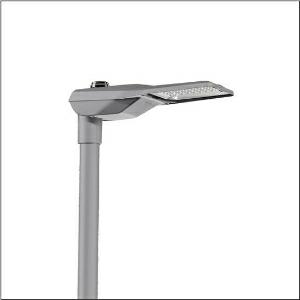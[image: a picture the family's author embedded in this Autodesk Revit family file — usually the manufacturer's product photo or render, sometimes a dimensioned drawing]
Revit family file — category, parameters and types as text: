
# Revit family: streetlight_sl_21_mini___st0_5a_5xe6b47n08hb_7d81
name_source: partatom
category: Lighting Fixtures
units: mm (PartAtom-declared; Revit-internal decimal feet)

## family parameters
Cut with Voids When Loaded = No
Host = Face
Light Source = No
Part Type = Normal
Room Calculation Point = No
Round Connector Dimension = Use Diameter
Shared = No

## types (1)
- --- (1 x LED, 9430 lm, 66 W, 4000K)
    Apparent Load = 66 VA
    CIE Flux Codes = 41 75 97 100 100
    Color Rendering = 70
    Color Temperature = 4000K
    Default Elevation = 1800 mm
    Description = Streetlight SL 21 mini, mast luminaire, primary light control with lens, of PMMA, primary optical cover: cover, of toughened safety glass, transparent, light distribution: ST0.5a, light emission: direct distribution, primary light characteristic: asymmetric, installation type: side-entry, LED, 3G 1.5mm², High Power LED, rated luminous flux: 9.430lm, luminous efficacy: 143lm/W, light colour: 740, colour temperature: 4000K, control gear: NEMA (7pin), control: overheat protection, pre-setting: linear dimming characteristic, constant luminous flux control, time-dependent luminous flux control, flexible luminous flux parameterisation, mains connection: 230..240V, AC, 50/60Hz, connection cable pre-assembled, cable length: 8,5m, wiring characteristics: H07RN-F, start of lifetime: 66W, end of service life: 69W, reduction: 30W, luminaire housing, of diecast aluminium (EN AC-44300), powder-coated, SITECO metallic grey (DB 702S), corrosivity category C5 high according to DIN EN ISO 12944, multi-level sealing system, sealing non-destructively replaceable, inclination adjustable: 0°, 5°, 10°, 15°, length: 628mm, width: 235mm, height: 110mm, spigot size: 42mm (side-entry), mounting height: 4..8m, protection rating (complete): IP66, insulation class (complete): insulation class I (protective earthing), certification: CE, ENEC, ENEC+, VDE, impact resistance: IK10, permissible operating ambient temperature for outdoor applications: -40..+50°C, standard-compliant lighting for roads and squares, packaging unit: 1 piece

Light Distribution: ST0.5a
    Height = 110 mm
    Lamp = 1 x LED
    Lamp Light Flux = 9430 lm
    Lamp Power = 66 W
    Lamp count = 1
    Length = 625 mm
    Luminous efficacy = 143 lm/W
    Manufacturer = Siteco
    ModVariant = No
    Model = 5XE6B47N08HB
    Number of Poles = 1
    OnlyDefault = Yes
    Power Factor = 1
    Product Name = Streetlight SL 21 mini | ST0.5a
    Product group = mast luminaire | pylon top
    ProductGroupID = 6100
    Protection Class = Protection class I
    Protection Degree = IP 66
    RLX_Detail_Level = 1
    RLX_Emergency_Light_Flux = 0 lm
    RLX_Emergency_Type = 0
    RLX_Emergency_Type_DB = No
    RlxData = <blob elided: 37161 chars, md5=1969a951>
    Socket = socket
    Standby Power = 0 W
    System Light Flux = 9430 lm
    System Power = 66 W
    Type Comments = factory setting: luminous flux: 100 % | dim-lin: 254 | 670 mA
    Type Image = l_1294379.jpg
    URL = http://relux.com
    VarID = @adj_136913
    Voltage = 0 V
    Weight = 0.00 kg
    Width = 234 mm

## geometry (parser evidence)
native form markers: Blend x4, Sweep x12
no freeform markers — native parametric forms only
